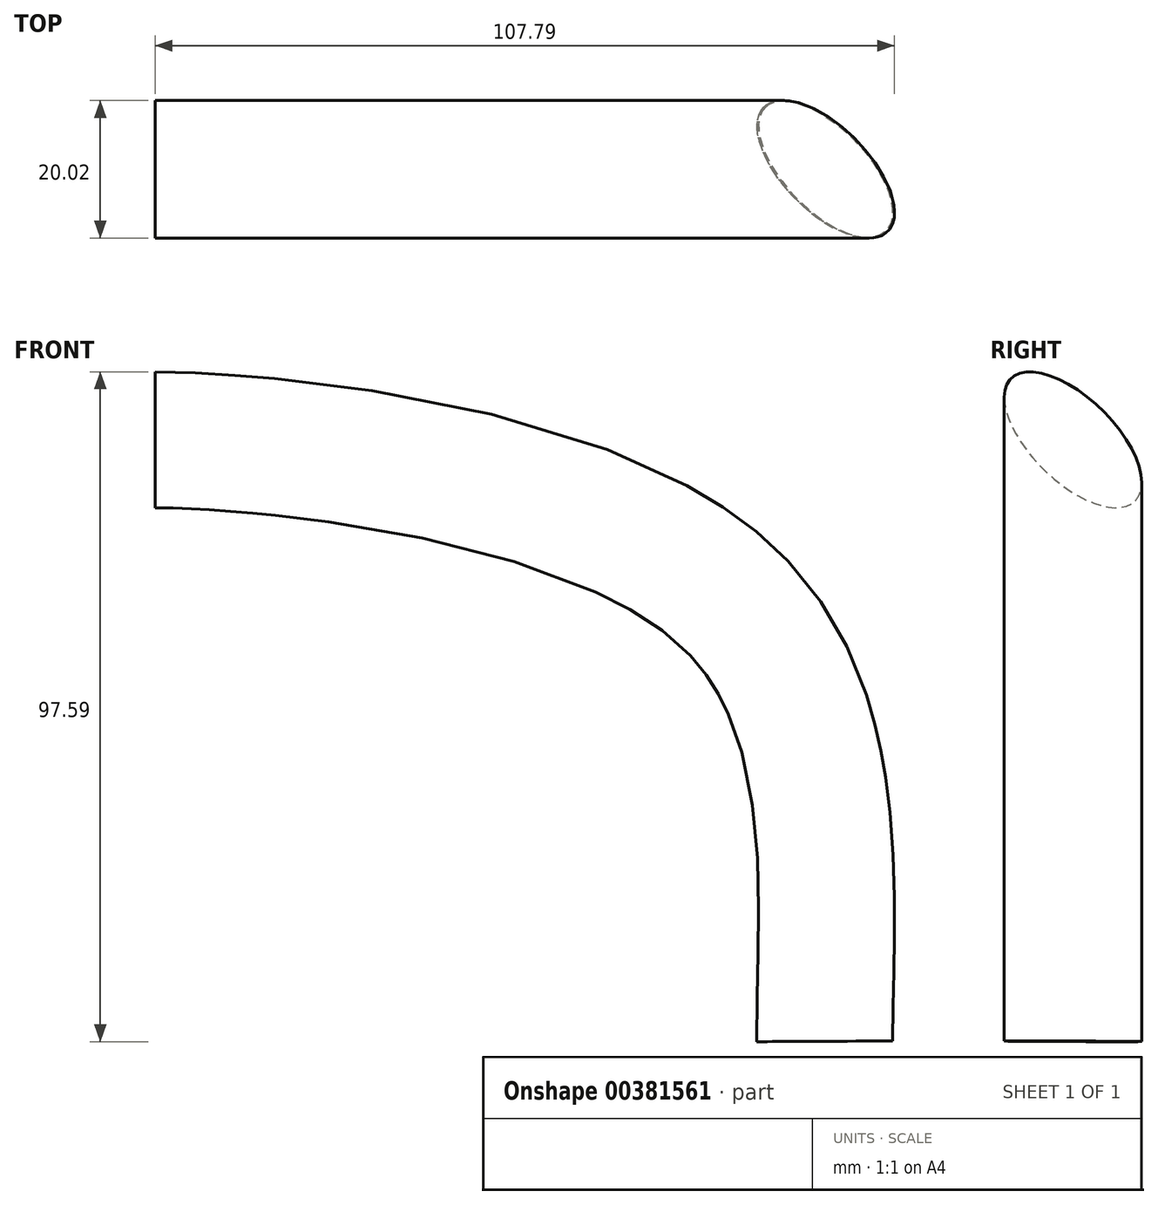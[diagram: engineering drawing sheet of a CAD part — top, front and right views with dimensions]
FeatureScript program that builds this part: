
annotation { "Feature Type Name" : "Feature", "Feature Type Description" : "" }
export const myFeature = defineFeature(function(context is Context, id is Id, definition is map)
    precondition{}
    {
        {
            var Q0;
            Q0=qCreatedBy(makeId("Front.planeOp"),FACE);
            var sketch = newSketch(context, id + "F0", { "sketchPlane" : qUnion([Q0])});
            skFitSpline(sketch, "E0", {"points": [v(-66.1, 87.64) * mm, v(16.8, 65.31) * mm, v(31.54, 0) * mm], "startDerivative": vector(71.87, 0) * mm, "endDerivative": vector(0.66, -128.02) * mm});
            skSolve(sketch);
        }
        {
            var Q0;
            Q0=sQuery(id+"F0.wireOp",VERTEX,"E0.2.internal");
            var Q1;
            Q1=sQuery(id+"F0.wireOp",EDGE,"E0");
            cPlane(context, id + "F1", {"entities" : qUnion([Q0, Q1]), "cplaneType" : CPlaneType.CURVE_POINT, "offset" : 25.4 * mm, "width" : 152.4 * mm, "height" : 152.4 * mm});
        }
        {
            var Q0;
            Q0=qCreatedBy(id+"F1.planeOp",FACE);
            var sketch = newSketch(context, id + "F2", { "sketchPlane" : qUnion([Q0])});
            skPoint(sketch, "E1.center.orphan", {"position": v(31.54, 0) * mm});
            skEllipse(sketch, "E2", {"center": v(31.54, 0) * mm, "majorRadius": 12.7 * mm, "minorRadius": 6.08 * mm, "majorAxis": v(-0.7, -0.71)});
            skFitSpline(sketch, "E3.0", {"points": [v(23.84, -7.54) * mm, v(23.97, -7.7) * mm, v(24.13, -7.83) * mm, v(24.43, -7.99) * mm, v(24.9, -8.1) * mm, v(25.6, -8.1) * mm, v(26.41, -8.01) * mm, v(27.63, -7.68) * mm, v(29.01, -7.07) * mm, v(30.18, -6.4) * mm, v(31.37, -5.65) * mm, v(32.55, -4.75) * mm, v(33.7, -3.74) * mm, v(34.53, -2.93) * mm, v(35.32, -2.09) * mm, v(36.31, -0.92) * mm, v(37.19, 0.27) * mm, v(37.93, 1.47) * mm, v(38.57, 2.65) * mm, v(39.16, 4.04) * mm, v(39.46, 5.26) * mm, v(39.55, 6.08) * mm, v(39.53, 6.77) * mm, v(39.4, 7.25) * mm, v(39.25, 7.54) * mm, v(39.12, 7.7) * mm, v(38.95, 7.83) * mm, v(38.66, 7.99) * mm, v(38.18, 8.1) * mm, v(37.49, 8.1) * mm, v(36.67, 8.01) * mm, v(35.46, 7.68) * mm, v(34.07, 7.07) * mm, v(32.9, 6.4) * mm, v(31.72, 5.65) * mm, v(30.54, 4.75) * mm, v(29.4, 3.74) * mm, v(28.56, 2.93) * mm, v(27.76, 2.09) * mm, v(26.77, 0.92) * mm, v(25.9, -0.27) * mm, v(25.16, -1.47) * mm, v(24.52, -2.65) * mm, v(23.93, -4.04) * mm, v(23.62, -5.26) * mm, v(23.54, -6.08) * mm, v(23.55, -6.77) * mm, v(23.68, -7.25) * mm, v(23.84, -7.54) * mm, v(23.97, -7.7) * mm, v(24.13, -7.83) * mm, v(23.84, -7.54) * mm]});
            skSolve(sketch);
        }
        {
            var Q0;
            Q0=makeQuery(id+"F2.imprint","IMPRINT",FACE,{"disambiguationData":[TD([[makeQuery(id+"F2.imprint","IMPRINT",EDGE,{"derivedFrom":sQuery(id+"F2.wireOp",EDGE,"E2")}),1.0]])]});
            var Q1;
            Q1=sQuery(id+"F0.wireOp",EDGE,"E0");
            sweep(context, id + "F3", {"profiles" : qUnion([Q0]), "path" : qUnion([Q1])});
        }
    });
